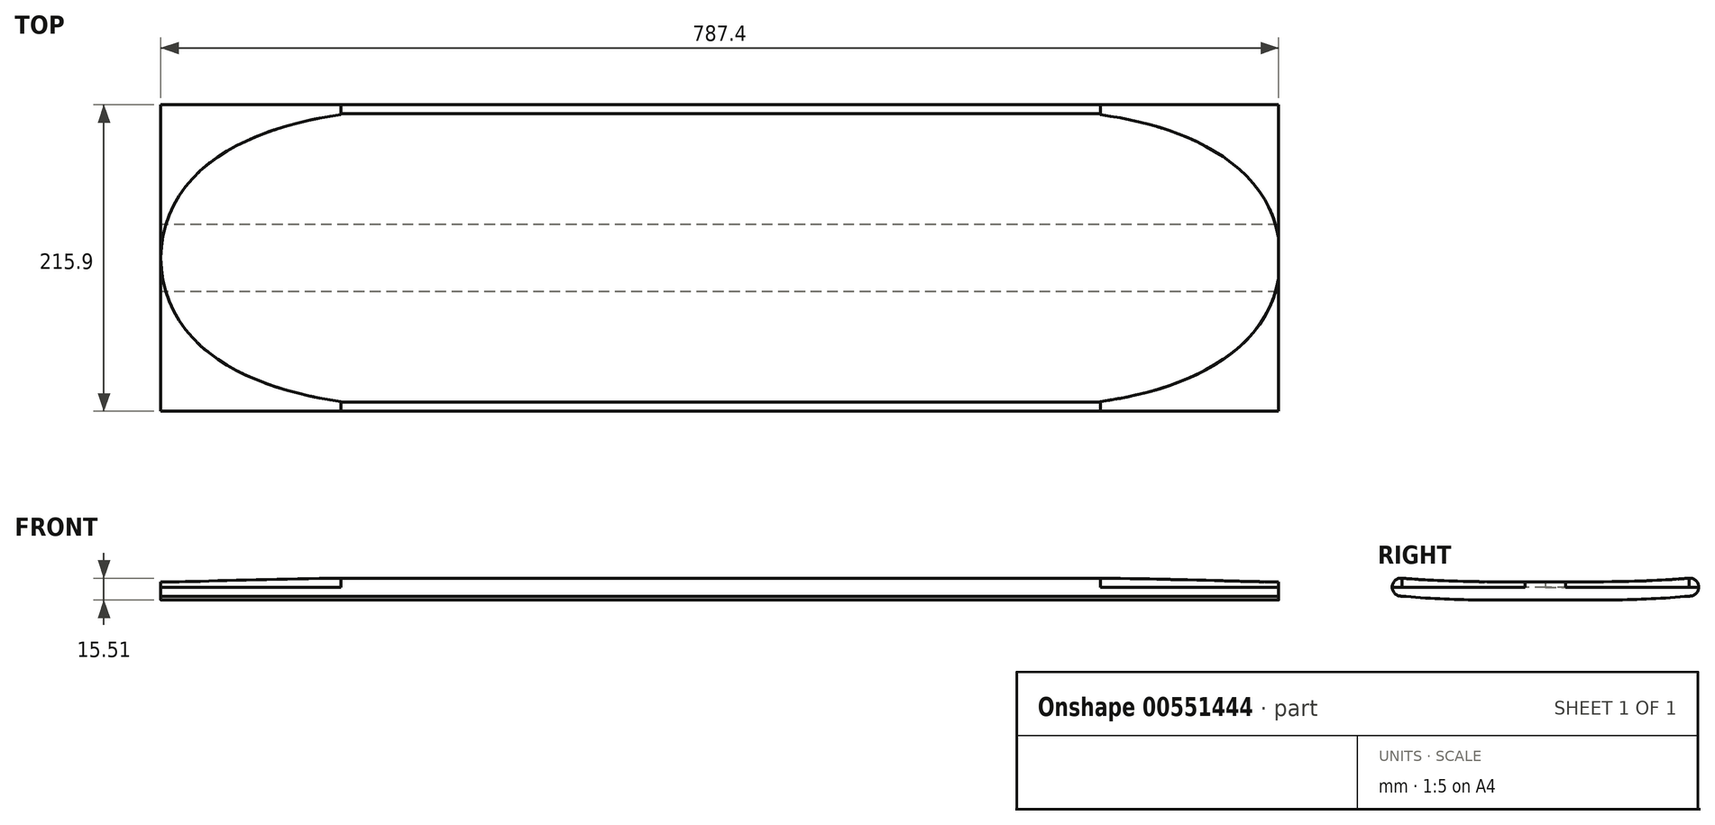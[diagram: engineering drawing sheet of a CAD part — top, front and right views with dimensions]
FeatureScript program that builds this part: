
annotation { "Feature Type Name" : "Feature", "Feature Type Description" : "" }
export const myFeature = defineFeature(function(context is Context, id is Id, definition is map)
    precondition{}
    {
        {
            var Q0;
            Q0=qCreatedBy(makeId("Right.planeOp"),FACE);
            var sketch = newSketch(context, id + "F0", { "sketchPlane" : qUnion([Q0])});
            skLineSegment(sketch, "E0.left", {"start": v(-107.95, 0) * mm, "end": v(-107.95, 0) * mm});
            skLineSegment(sketch, "E0.right", {"start": v(107.95, 0) * mm, "end": v(107.95, 0) * mm});
            skPoint(sketch, "E0.middle", {"position": v(0, 0) * mm});
            skPoint(sketch, "E1.visualSharp", {"position": v(107.95, 6.35) * mm});
            skArc(sketch, "E1.filletArc", {"start": v(107.95, 0) * mm, "mid": v(106.1, 4.5) * mm, "end": v(101.6, 6.35) * mm});
            skPoint(sketch, "E2.visualSharp", {"position": v(107.95, -6.35) * mm});
            skArc(sketch, "E2.filletArc", {"start": v(101.6, -6.35) * mm, "mid": v(106.1, -4.5) * mm, "end": v(107.95, 0) * mm});
            skPoint(sketch, "E3.visualSharp", {"position": v(-107.95, 6.35) * mm});
            skArc(sketch, "E3.filletArc", {"start": v(-101.6, 6.35) * mm, "mid": v(-106.1, 4.5) * mm, "end": v(-107.95, 0) * mm});
            skPoint(sketch, "E4.visualSharp", {"position": v(-107.95, -6.35) * mm});
            skArc(sketch, "E4.filletArc", {"start": v(-107.95, 0) * mm, "mid": v(-106.1, -4.5) * mm, "end": v(-101.6, -6.35) * mm});
            skPoint(sketch, "E5.center.orphan", {"position": v(0, 6.35) * mm});
            skPoint(sketch, "E6.center.orphan", {"position": v(0, -6.35) * mm});
            skLineSegment(sketch, "E7", {"start": v(0, 6.35) * mm, "end": v(0, -16.13) * mm, "construction": true});
            skFitSpline(sketch, "E8", {"points": [v(-101.6, 6.35) * mm, v(0, 3.56) * mm], "startDerivative": vector(99.66, -8.83) * mm, "endDerivative": vector(103.67, -0.32) * mm});
            skFitSpline(sketch, "E9", {"points": [v(-101.6, -6.35) * mm, v(0, -8.5) * mm], "startDerivative": vector(102.55, -8.8) * mm, "endDerivative": vector(103.62, 3.77) * mm});
            skFitSpline(sketch, "E10.MirrorCS", {"points": [v(101.6, -6.35) * mm, v(0, -8.5) * mm], "startDerivative": vector(-102.55, -8.8) * mm, "endDerivative": vector(-103.62, 3.77) * mm});
            skFitSpline(sketch, "E11.MirrorCS", {"points": [v(101.6, 6.35) * mm, v(0, 3.56) * mm], "startDerivative": vector(-99.66, -8.83) * mm, "endDerivative": vector(-103.67, -0.32) * mm});
            skPoint(sketch, "E12", {"position": v(23.79, -9.1) * mm});
            skLineSegment(sketch, "E13", {"start": v(23.79, -9.1) * mm, "end": v(-23.79, -9.1) * mm});
            skSolve(sketch);
        }
        {
            var Q0;
            Q0=qSketchRegion(id+"F0",true);
            extrude(context, id + "F1", {"entities" : qUnion([Q0]), "depth" : 787.4 * mm, "offsetDistance" : 25.4 * mm});
        }
        {
            var Q0;
            Q0=qCreatedBy(makeId("Top.planeOp"),FACE);
            var sketch = newSketch(context, id + "F2", { "sketchPlane" : qUnion([Q0])});
            skFitSpline(sketch, "E14", {"points": [v(0, 0) * mm, v(126.82, 101.05) * mm], "startDerivative": vector(3.63, 195.56) * mm, "endDerivative": vector(183.12, 25.53) * mm});
            skFitSpline(sketch, "E15.MirrorCS", {"points": [v(0, 0) * mm, v(126.82, -101.05) * mm], "startDerivative": vector(3.63, -195.56) * mm, "endDerivative": vector(183.12, -25.53) * mm});
            skFitSpline(sketch, "E16.MirrorCS", {"points": [v(788.77, 0) * mm, v(661.95, -101.05) * mm], "startDerivative": vector(-3.63, -195.56) * mm, "endDerivative": vector(-183.12, -25.53) * mm});
            skFitSpline(sketch, "E17.MirrorCS", {"points": [v(788.77, 0) * mm, v(661.95, 101.05) * mm], "startDerivative": vector(-3.63, 195.56) * mm, "endDerivative": vector(-183.12, 25.53) * mm});
            skLineSegment(sketch, "E18", {"start": v(661.95, 101.05) * mm, "end": v(661.95, 174.56) * mm});
            skLineSegment(sketch, "E19", {"start": v(661.95, 174.56) * mm, "end": v(925.62, 174.56) * mm});
            skLineSegment(sketch, "E20", {"start": v(925.62, 174.56) * mm, "end": v(925.62, -210.46) * mm});
            skLineSegment(sketch, "E21", {"start": v(925.62, -210.46) * mm, "end": v(661.95, -210.46) * mm});
            skLineSegment(sketch, "E22", {"start": v(661.95, -210.46) * mm, "end": v(661.95, -101.05) * mm});
            skLineSegment(sketch, "E23", {"start": v(126.82, 101.05) * mm, "end": v(126.82, 193.44) * mm});
            skLineSegment(sketch, "E24", {"start": v(126.82, 193.44) * mm, "end": v(-168.91, 193.44) * mm});
            skLineSegment(sketch, "E25", {"start": v(-168.91, 193.44) * mm, "end": v(-168.91, -217.45) * mm});
            skLineSegment(sketch, "E26", {"start": v(-168.91, -217.45) * mm, "end": v(126.82, -217.45) * mm});
            skLineSegment(sketch, "E27", {"start": v(126.82, -217.45) * mm, "end": v(126.82, -101.05) * mm});
            skSolve(sketch);
        }
        {
            var Q0;
            Q0=makeQuery(id+"F2.imprint","IMPRINT",FACE,{"disambiguationData":[TD([[makeQuery(id+"F2.imprint","IMPRINT",EDGE,{"derivedFrom":sQuery(id+"F2.wireOp",EDGE,"E16.MirrorCS")}),1.0]])]});
            var Q1;
            Q1=makeQuery(id+"F2.imprint","IMPRINT",FACE,{"disambiguationData":[TD([[makeQuery(id+"F2.imprint","IMPRINT",EDGE,{"derivedFrom":sQuery(id+"F2.wireOp",EDGE,"E14")}),1.0]])]});
            extrude(context, id + "F3", {"entities" : qUnion([Q0, Q1]), "operationType" : NewBodyOperationType.REMOVE, "endBound" : BoundingType.THROUGH_ALL, "depth" : 25.4 * mm, "offsetDistance" : 25.4 * mm});
        }
    });
